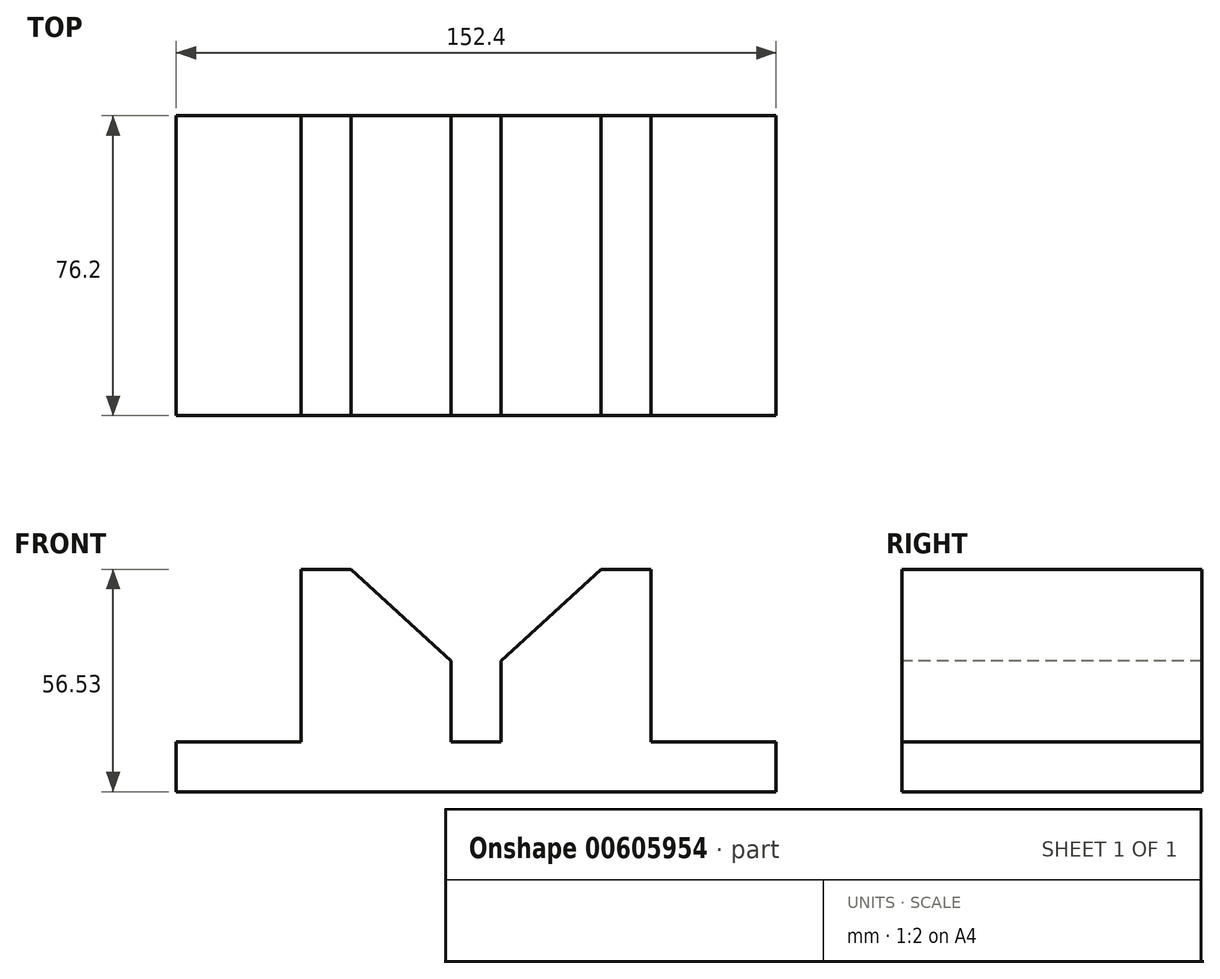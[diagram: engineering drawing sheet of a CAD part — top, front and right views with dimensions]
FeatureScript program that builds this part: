
annotation { "Feature Type Name" : "Feature", "Feature Type Description" : "" }
export const myFeature = defineFeature(function(context is Context, id is Id, definition is map)
    precondition{}
    {
        {
            var Q0;
            Q0=qCreatedBy(makeId("Front.planeOp"),FACE);
            var sketch = newSketch(context, id + "F0", { "sketchPlane" : qUnion([Q0])});
            skLineSegment(sketch, "E0", {"start": v(0, 0) * mm, "end": v(0, 12.7) * mm});
            skLineSegment(sketch, "E1", {"start": v(0, 12.7) * mm, "end": v(31.75, 12.7) * mm});
            skLineSegment(sketch, "E2", {"start": v(31.75, 12.7) * mm, "end": v(31.75, 56.53) * mm});
            skLineSegment(sketch, "E3", {"start": v(31.75, 56.53) * mm, "end": v(44.45, 56.53) * mm});
            skLineSegment(sketch, "E4", {"start": v(44.45, 56.53) * mm, "end": v(69.85, 33.19) * mm});
            skLineSegment(sketch, "E5", {"start": v(69.85, 33.19) * mm, "end": v(69.85, 12.7) * mm});
            skLineSegment(sketch, "E6", {"start": v(69.85, 12.7) * mm, "end": v(82.55, 12.7) * mm});
            skLineSegment(sketch, "E7", {"start": v(82.55, 12.7) * mm, "end": v(82.55, 33.19) * mm});
            skLineSegment(sketch, "E8", {"start": v(82.55, 33.19) * mm, "end": v(107.95, 56.53) * mm});
            skLineSegment(sketch, "E9", {"start": v(107.95, 56.53) * mm, "end": v(120.65, 56.53) * mm});
            skLineSegment(sketch, "E10", {"start": v(120.65, 56.53) * mm, "end": v(120.65, 12.7) * mm});
            skLineSegment(sketch, "E11", {"start": v(120.65, 12.7) * mm, "end": v(152.4, 12.7) * mm});
            skLineSegment(sketch, "E12", {"start": v(152.4, 12.7) * mm, "end": v(152.4, 0) * mm});
            skLineSegment(sketch, "E13", {"start": v(152.4, 0) * mm, "end": v(0, 0) * mm});
            skSolve(sketch);
        }
        {
            var Q0;
            Q0=makeQuery(id+"F0.imprint","IMPRINT",FACE,{"disambiguationData":[TD([[makeQuery(id+"F0.imprint","IMPRINT",EDGE,{"derivedFrom":sQuery(id+"F0.wireOp",EDGE,"E0")}),-1.0]])]});
            extrude(context, id + "F1", {"entities" : qUnion([Q0]), "oppositeDirection" : true, "depth" : 76.2 * mm, "offsetDistance" : 25.4 * mm});
        }
    });
